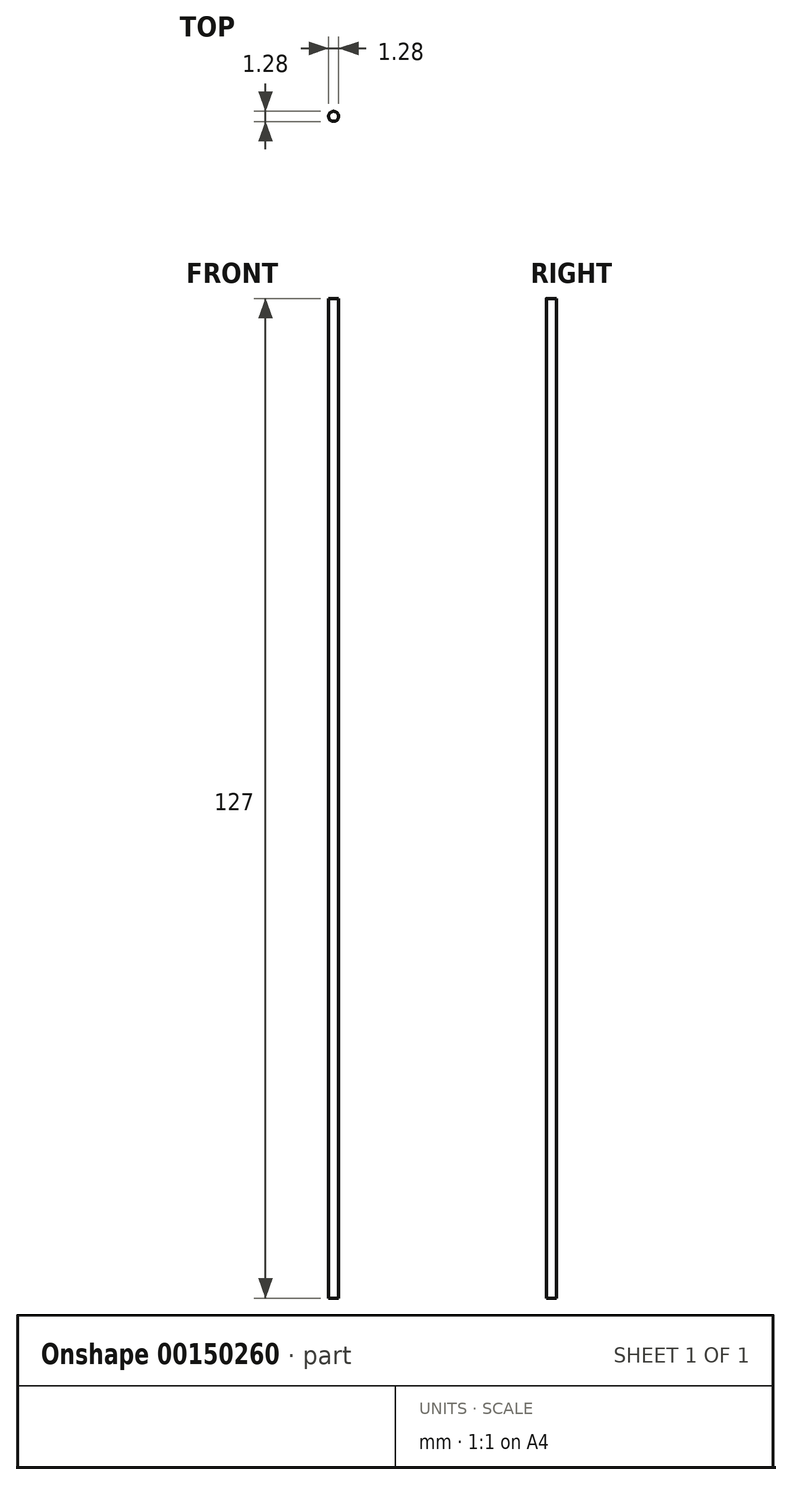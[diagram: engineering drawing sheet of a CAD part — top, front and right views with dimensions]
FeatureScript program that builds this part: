
annotation { "Feature Type Name" : "Feature", "Feature Type Description" : "" }
export const myFeature = defineFeature(function(context is Context, id is Id, definition is map)
    precondition{}
    {
        {
            var Q0;
            Q0=qCreatedBy(makeId("Top.planeOp"),FACE);
            var sketch = newSketch(context, id + "F0", { "sketchPlane" : qUnion([Q0])});
            skCircle(sketch, "E0", {"center": v(0, 0) * mm, "radius": 0.64 * mm});
            skSolve(sketch);
        }
        {
            var Q0;
            Q0 = qSketchRegion(id + "F0", true);
            extrude(context, id + "F1", {"entities" : qUnion([Q0]), "depth" : 127 * mm});
        }
    });
